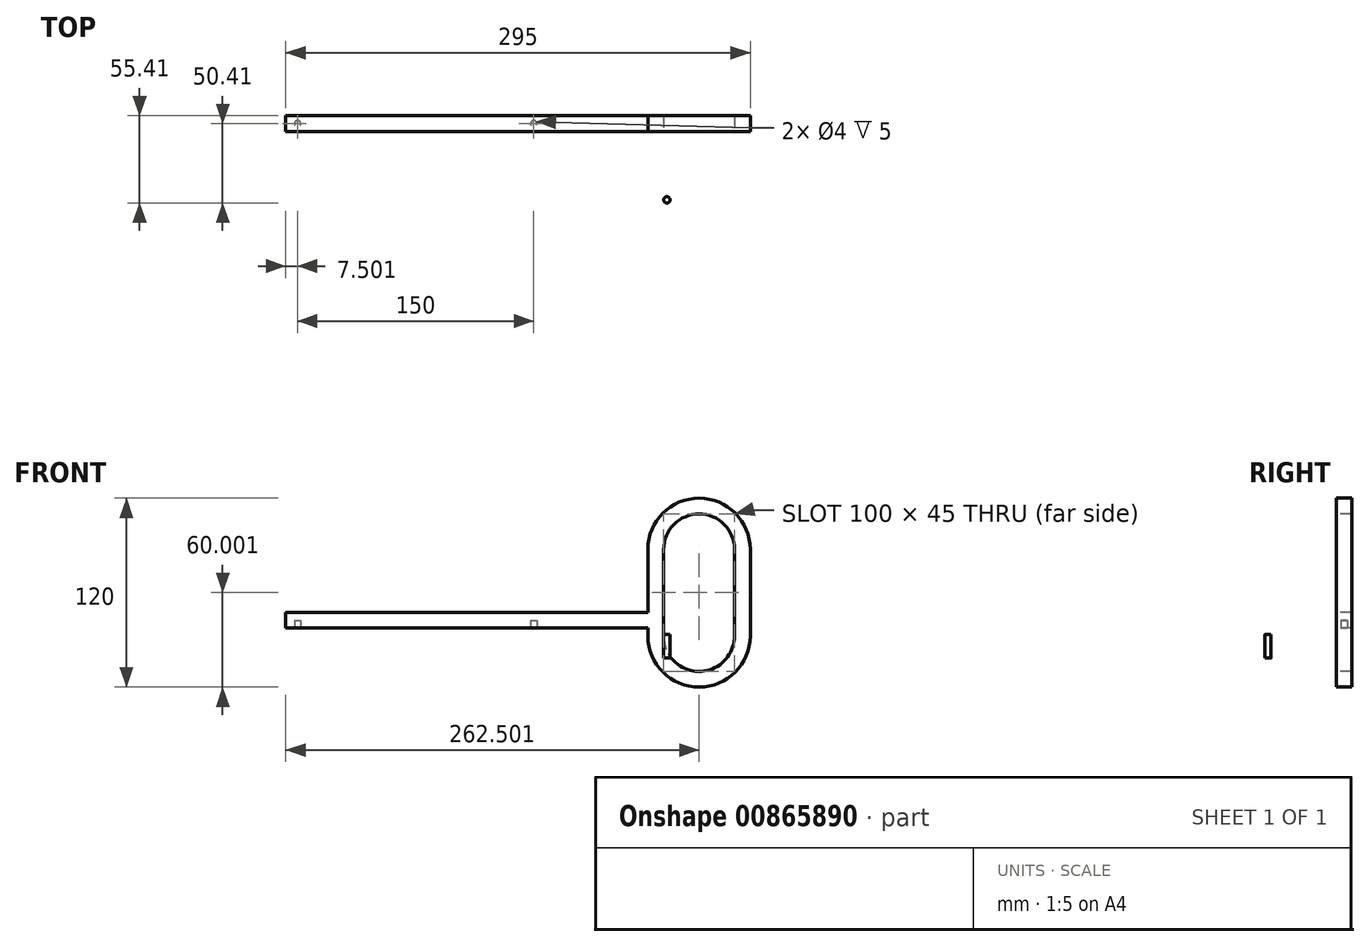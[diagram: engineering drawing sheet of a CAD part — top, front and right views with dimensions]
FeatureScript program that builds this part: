
annotation { "Feature Type Name" : "Feature", "Feature Type Description" : "" }
export const myFeature = defineFeature(function(context is Context, id is Id, definition is map)
    precondition{}
    {
        {
            var Q0;
            Q0=qCreatedBy(makeId("Front.planeOp"),FACE);
            var sketch = newSketch(context, id + "F0", { "sketchPlane" : qUnion([Q0])});
            skArc(sketch, "E0", {"start": v(-10.59, 41.6) * mm, "mid": v(-27.9, 101.6) * mm, "end": v(-45.23, 41.6) * mm});
            skArc(sketch, "E1", {"start": v(-45.23, 41.6) * mm, "mid": v(-27.9, -18.4) * mm, "end": v(-10.59, 41.6) * mm});
            skLineSegment(sketch, "E2", {"start": v(-60.4, 69.1) * mm, "end": v(-60.4, 14.1) * mm});
            skLineSegment(sketch, "E3", {"start": v(4.6, 69.1) * mm, "end": v(4.6, 14.1) * mm});
            skSolve(sketch);
        }
        {
            var Q0;
            Q0=qSketchRegion(id+"F0",true);
            extrude(context, id + "F1", {"entities" : qUnion([Q0]), "depth" : 10 * mm, "offsetDistance" : 25 * mm});
        }
        {
            var Q0;
            Q0=makeQuery(id+"F1.opExtrude","CAP_FACE",FACE,{"disambiguationData":[OSD([sQuery(id+"F0.wireOp",EDGE,"E0"),sQuery(id+"F0.wireOp",EDGE,"E1"),sQuery(id+"F0.wireOp",EDGE,"E2"),sQuery(id+"F0.wireOp",EDGE,"E3")])],"isStart":false});
            var sketch = newSketch(context, id + "F2", { "sketchPlane" : qUnion([Q0])});
            skArc(sketch, "E4", {"start": v(-50.4, 69.1) * mm, "mid": v(-27.9, 91.6) * mm, "end": v(-5.4, 69.1) * mm});
            skArc(sketch, "E5", {"start": v(-50.4, 14.1) * mm, "mid": v(-27.9, -8.4) * mm, "end": v(-5.4, 14.1) * mm});
            skLineSegment(sketch, "E6", {"start": v(-50.4, 69.1) * mm, "end": v(-50.4, 14.1) * mm});
            skLineSegment(sketch, "E7", {"start": v(-5.4, 69.1) * mm, "end": v(-5.4, 14.1) * mm});
            skSolve(sketch);
        }
        {
            var Q0;
            Q0=qSketchRegion(id+"F2",true);
            extrude(context, id + "F3", {"entities" : qUnion([Q0]), "operationType" : NewBodyOperationType.REMOVE, "endBound" : BoundingType.THROUGH_ALL, "oppositeDirection" : true, "depth" : 25 * mm, "offsetDistance" : 25 * mm});
        }
        {
            var Q0;
            Q0=makeQuery(id+"F1.opExtrude","SWEPT_FACE",FACE,{"disambiguationData":[OSD([sQuery(id+"F0.wireOp",EDGE,"E2")])]});
            var sketch = newSketch(context, id + "F4", { "sketchPlane" : qUnion([Q0])});
            skLineSegment(sketch, "E8.bottom", {"start": v(0, 29.1) * mm, "end": v(10, 29.1) * mm});
            skLineSegment(sketch, "E8.top", {"start": v(0, 19.1) * mm, "end": v(10, 19.1) * mm});
            skLineSegment(sketch, "E8.left", {"start": v(0, 29.1) * mm, "end": v(0, 19.1) * mm});
            skLineSegment(sketch, "E8.right", {"start": v(10, 29.1) * mm, "end": v(10, 19.1) * mm});
            skSolve(sketch);
        }
        {
            var Q0;
            Q0=qSketchRegion(id+"F4",true);
            extrude(context, id + "F5", {"entities" : qUnion([Q0]), "operationType" : NewBodyOperationType.ADD, "depth" : 230 * mm, "offsetDistance" : 25 * mm});
        }
        {
            var Q0;
            Q0=makeQuery(id+"F5.opExtrude","SWEPT_FACE",FACE,{"disambiguationData":[OSD([sQuery(id+"F4.wireOp",EDGE,"E8.top")])]});
            var sketch = newSketch(context, id + "F6", { "sketchPlane" : qUnion([Q0])});
            skCircle(sketch, "E9", {"center": v(-132.9, 5) * mm, "radius": 2 * mm});
            skCircle(sketch, "E10", {"center": v(-282.9, 5) * mm, "radius": 2 * mm});
            skSolve(sketch);
        }
        {
            var Q0;
            Q0=qSketchRegion(id+"F6",true);
            extrude(context, id + "F7", {"entities" : qUnion([Q0]), "operationType" : NewBodyOperationType.REMOVE, "oppositeDirection" : true, "depth" : 5 * mm, "offsetDistance" : 25 * mm});
        }
        {
            var Q0;
            Q0=qCreatedBy(makeId("Top.planeOp"),FACE);
            var sketch = newSketch(context, id + "F8", { "sketchPlane" : qUnion([Q0])});
            skCircle(sketch, "E11", {"center": v(-48.36, -53.41) * mm, "radius": 2 * mm});
            skSolve(sketch);
        }
        {
            var Q0;
            Q0 = qSketchRegion(id + "F8", true);
            extrude(context, id + "F9", {"entities" : qUnion([Q0]), "depth" : 15 * mm, "offsetDistance" : 25 * mm});
        }
    });
